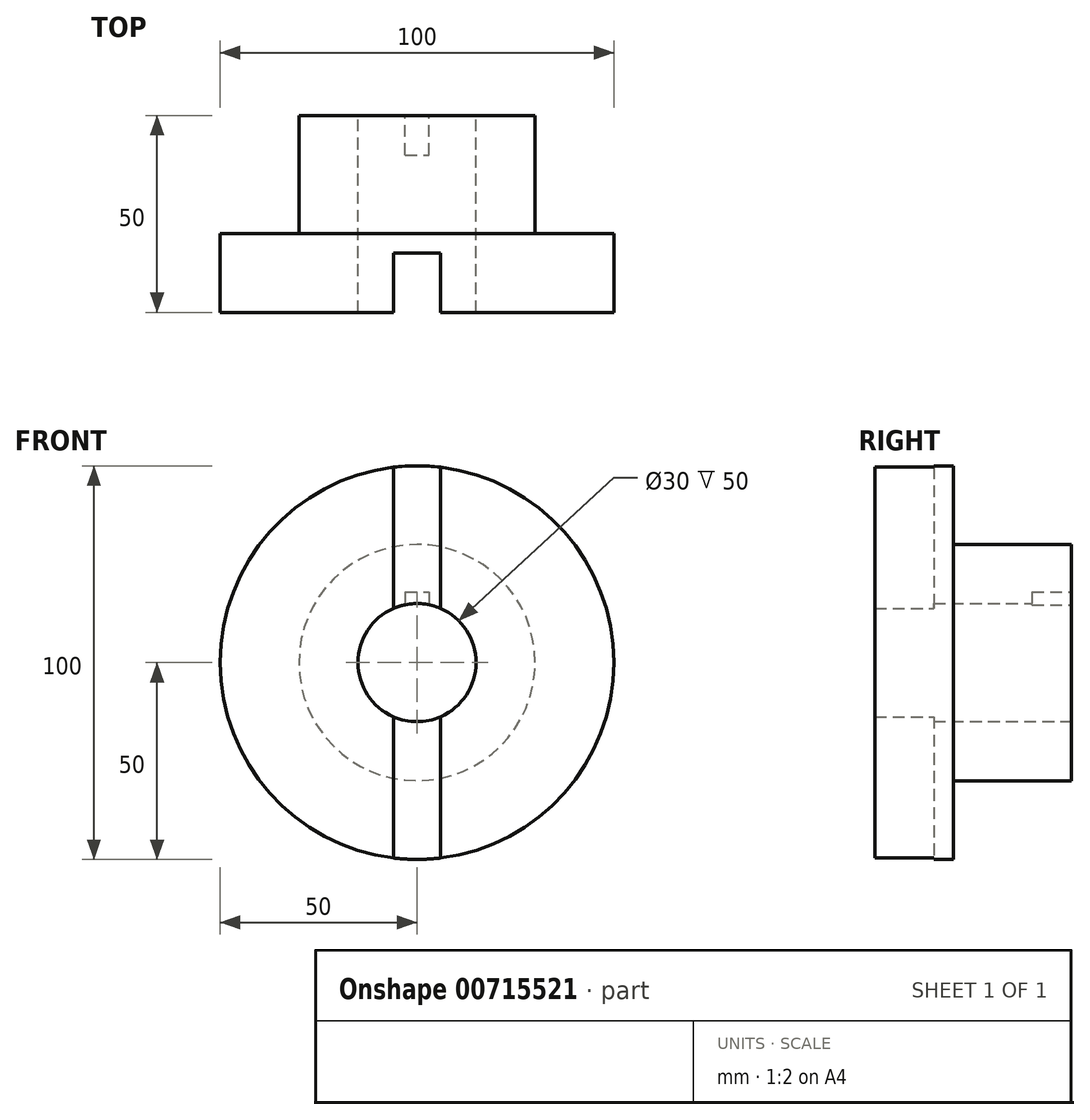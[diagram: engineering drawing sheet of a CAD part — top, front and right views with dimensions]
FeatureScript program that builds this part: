
annotation { "Feature Type Name" : "Feature", "Feature Type Description" : "" }
export const myFeature = defineFeature(function(context is Context, id is Id, definition is map)
    precondition{}
    {
        {
            var Q0;
            Q0=qCreatedBy(makeId("Top.planeOp"),FACE);
            var sketch = newSketch(context, id + "F0", { "sketchPlane" : qUnion([Q0])});
            skLineSegment(sketch, "E0", {"start": v(0, -30.95) * mm, "end": v(0, 19.05) * mm});
            skLineSegment(sketch, "E1", {"start": v(0, 19.05) * mm, "end": v(30, 19.05) * mm});
            skLineSegment(sketch, "E2", {"start": v(30, 19.05) * mm, "end": v(30, -10.95) * mm});
            skLineSegment(sketch, "E3", {"start": v(30, -10.95) * mm, "end": v(50, -10.95) * mm});
            skLineSegment(sketch, "E4", {"start": v(50, -10.95) * mm, "end": v(50, -30.95) * mm});
            skLineSegment(sketch, "E5", {"start": v(50, -30.95) * mm, "end": v(0, -30.95) * mm});
            skSolve(sketch);
        }
        {
            var Q0;
            Q0=makeQuery(id+"F0.imprint","IMPRINT",FACE,{"disambiguationData":[TD([[makeQuery(id+"F0.imprint","IMPRINT",EDGE,{"derivedFrom":sQuery(id+"F0.wireOp",EDGE,"E0")}),-1.0]])]});
            var Q1;
            Q1=sQuery(id+"F0.wireOp",EDGE,"E0");
            revolve(context, id + "F1", {"surfaceOperationType" : NewSurfaceOperationType.NEW, "entities" : qUnion([Q0]), "axis" : qUnion([Q1]), "revolveType" : RevolveType.FULL});
        }
        {
            var Q0;
            Q0=makeQuery(id+"F1.opRevolve","SWEPT_FACE",FACE,{"disambiguationData":[OSD([sQuery(id+"F0.wireOp",EDGE,"E5")])]});
            var sketch = newSketch(context, id + "F2", { "sketchPlane" : qUnion([Q0])});
            skLineSegment(sketch, "E6.bottom", {"start": v(-6, 60) * mm, "end": v(6, 60) * mm});
            skLineSegment(sketch, "E6.top", {"start": v(-6, -60) * mm, "end": v(6, -60) * mm});
            skLineSegment(sketch, "E6.left", {"start": v(-6, 60) * mm, "end": v(-6, -60) * mm});
            skLineSegment(sketch, "E6.right", {"start": v(6, 60) * mm, "end": v(6, -60) * mm});
            skPoint(sketch, "E6.middle", {"position": v(0, 0) * mm});
            skSolve(sketch);
        }
        {
            var Q0;
            {var subQ0=sQuery(id+"F2.wireOp",EDGE,"E6.left");var subQ1=makeQuery(id+"F1.opRevolve","SWEPT_EDGE",EDGE,{"disambiguationData":[OSD([sQuery(id+"F0.wireOp",EDGE,"E4"),sQuery(id+"F0.wireOp",EDGE,"E5")])]});var subQ2=makeQuery(id+"F2.imprint","INTERSECT",VERTEX,{"disambiguationData":[OD(0.0)],"derivedFrom":[subQ1,subQ0]});Q0=makeQuery(id+"F2.imprint","IMPRINT",FACE,{"disambiguationData":[TD([[makeQuery(id+"F2.imprint","IMPRINT",EDGE,{"disambiguationData":[TD([[subQ2,-1.0]])],"derivedFrom":subQ0}),1.0]])]});}
            extrude(context, id + "F3", {"entities" : qUnion([Q0]), "operationType" : NewBodyOperationType.REMOVE, "oppositeDirection" : true, "depth" : 15 * mm, "offsetDistance" : 25 * mm});
        }
        {
            var Q0;
            Q0=makeQuery(id+"F1.opRevolve","SWEPT_FACE",FACE,{"disambiguationData":[OSD([sQuery(id+"F0.wireOp",EDGE,"E1")])]});
            var sketch = newSketch(context, id + "F4", { "sketchPlane" : qUnion([Q0])});
            skCircle(sketch, "E7", {"center": v(0, 0) * mm, "radius": 15 * mm});
            skSolve(sketch);
        }
        {
            var Q0;
            Q0=makeQuery(id+"F4.imprint","IMPRINT",FACE,{"disambiguationData":[TD([[makeQuery(id+"F4.imprint","IMPRINT",EDGE,{"derivedFrom":sQuery(id+"F4.wireOp",EDGE,"E7")}),1.0]])]});
            extrude(context, id + "F5", {"entities" : qUnion([Q0]), "operationType" : NewBodyOperationType.REMOVE, "oppositeDirection" : true, "depth" : 141 * mm, "offsetDistance" : 25 * mm});
        }
        {
            var Q0;
            Q0=makeQuery(id+"F1.opRevolve","SWEPT_FACE",FACE,{"disambiguationData":[OSD([sQuery(id+"F0.wireOp",EDGE,"E1")])]});
            var sketch = newSketch(context, id + "F6", { "sketchPlane" : qUnion([Q0])});
            skLineSegment(sketch, "E8.bottom", {"start": v(3, 18) * mm, "end": v(-3, 18) * mm});
            skLineSegment(sketch, "E8.top", {"start": v(3, 12) * mm, "end": v(-3, 12) * mm});
            skLineSegment(sketch, "E8.left", {"start": v(3, 18) * mm, "end": v(3, 12) * mm});
            skLineSegment(sketch, "E8.right", {"start": v(-3, 18) * mm, "end": v(-3, 12) * mm});
            skPoint(sketch, "E8.middle", {"position": v(0, 15) * mm});
            skSolve(sketch);
        }
        {
            var Q0;
            {var subQ0=sQuery(id+"F6.wireOp",EDGE,"E8.bottom");Q0=makeQuery(id+"F6.imprint","IMPRINT",FACE,{"disambiguationData":[TD([[makeQuery(id+"F6.imprint","IMPRINT",EDGE,{"derivedFrom":subQ0}),1.0]])]});}
            extrude(context, id + "F7", {"entities" : qUnion([Q0]), "operationType" : NewBodyOperationType.REMOVE, "oppositeDirection" : true, "depth" : 10 * mm, "offsetDistance" : 25 * mm});
        }
    });
